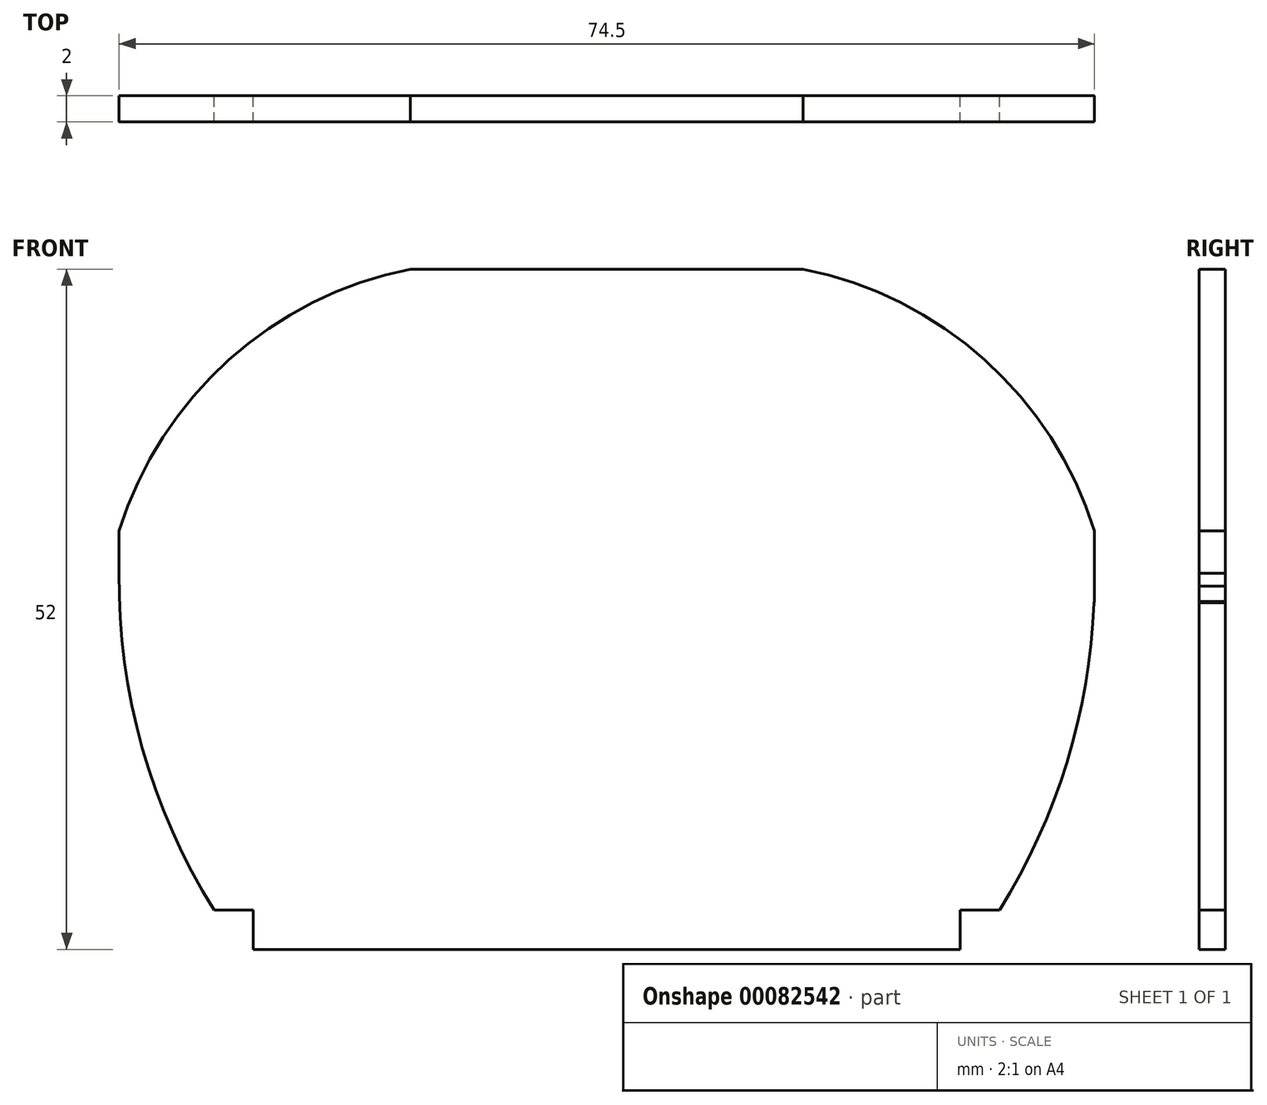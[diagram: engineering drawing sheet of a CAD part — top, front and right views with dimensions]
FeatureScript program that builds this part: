
annotation { "Feature Type Name" : "Feature", "Feature Type Description" : "" }
export const myFeature = defineFeature(function(context is Context, id is Id, definition is map)
    precondition{}
    {
        {
            var Q0;
            Q0=qCreatedBy(makeId("Front.planeOp"),FACE);
            var sketch = newSketch(context, id + "F0", { "sketchPlane" : qUnion([Q0])});
            skLineSegment(sketch, "E0", {"start": v(0, 0) * mm, "end": v(27, 0) * mm});
            skLineSegment(sketch, "E1", {"start": v(15, 52) * mm, "end": v(0, 52) * mm});
            skLineSegment(sketch, "E2", {"start": v(0, 52) * mm, "end": v(0, 0) * mm, "construction": true});
            skLineSegment(sketch, "E3", {"start": v(27, 0) * mm, "end": v(27, 3) * mm});
            skLineSegment(sketch, "E4", {"start": v(27, 3) * mm, "end": v(30, 3) * mm});
            skLineSegment(sketch, "E5", {"start": v(15, 52) * mm, "end": v(15, 22) * mm, "construction": true});
            skLineSegment(sketch, "E6", {"start": v(0, 0) * mm, "end": v(0, -22.64) * mm});
            skLineSegment(sketch, "E7", {"start": v(0, -22.64) * mm, "end": v(37.25, -22.64) * mm, "construction": true});
            skLineSegment(sketch, "E8", {"start": v(37.25, -22.64) * mm, "end": v(37.25, 57.14) * mm, "construction": true});
            skPoint(sketch, "E9.first.point", {"position": v(37.25, 32) * mm});
            skArc(sketch, "E10.trimOffspring", {"start": v(30, 3) * mm, "mid": v(35.83, 16.73) * mm, "end": v(37.14, 31.59) * mm});
            skLineSegment(sketch, "E11", {"start": v(15, 52) * mm, "end": v(15, 32) * mm, "construction": true});
            skLineSegment(sketch, "E12", {"start": v(15, 32) * mm, "end": v(56.61, 32) * mm, "construction": true});
            skArc(sketch, "E13", {"start": v(37.25, 32) * mm, "mid": v(28.88, 45.07) * mm, "end": v(15, 52) * mm});
            skLineSegment(sketch, "E14", {"start": v(37.25, 32) * mm, "end": v(37.25, 26.59) * mm});
            skLineSegment(sketch, "E15", {"start": v(37.25, 26.59) * mm, "end": v(37.22, 26.5) * mm});
            skLineSegment(sketch, "E16.MirrorCS", {"start": v(-37.25, 32) * mm, "end": v(-37.25, 26.59) * mm});
            skLineSegment(sketch, "E17.MirrorCS", {"start": v(-27, 0) * mm, "end": v(-27, 3) * mm});
            skLineSegment(sketch, "E18.MirrorCS", {"start": v(-27, 3) * mm, "end": v(-30, 3) * mm});
            skPoint(sketch, "E19.MirrorP", {"position": v(-37.25, 32) * mm});
            skLineSegment(sketch, "E20.MirrorCS", {"start": v(0, -22.64) * mm, "end": v(-37.25, -22.64) * mm, "construction": true});
            skLineSegment(sketch, "E21.MirrorCS", {"start": v(-37.25, -22.64) * mm, "end": v(-37.25, 57.14) * mm, "construction": true});
            skArc(sketch, "E22.MirrorCS", {"start": v(-30, 3) * mm, "mid": v(-35.83, 16.73) * mm, "end": v(-37.14, 31.59) * mm});
            skArc(sketch, "E23.MirrorCS", {"start": v(-37.25, 32) * mm, "mid": v(-28.88, 45.07) * mm, "end": v(-15, 52) * mm});
            skLineSegment(sketch, "E24.MirrorCS", {"start": v(-15, 52) * mm, "end": v(0, 52) * mm});
            skLineSegment(sketch, "E25.MirrorCS", {"start": v(-15, 52) * mm, "end": v(-15, 32) * mm, "construction": true});
            skLineSegment(sketch, "E26.MirrorCS", {"start": v(-15, 52) * mm, "end": v(-15, 22) * mm, "construction": true});
            skLineSegment(sketch, "E27.MirrorCS", {"start": v(-15, 32) * mm, "end": v(-56.61, 32) * mm, "construction": true});
            skLineSegment(sketch, "E28.MirrorCS", {"start": v(0, 0) * mm, "end": v(-27, 0) * mm});
            skSolve(sketch);
        }
        {
            var Q0;
            Q0 = qSketchRegion(id + "F0", true);
            extrude(context, id + "F1", {"entities" : qUnion([Q0]), "depth" : 2 * mm});
        }
    });
